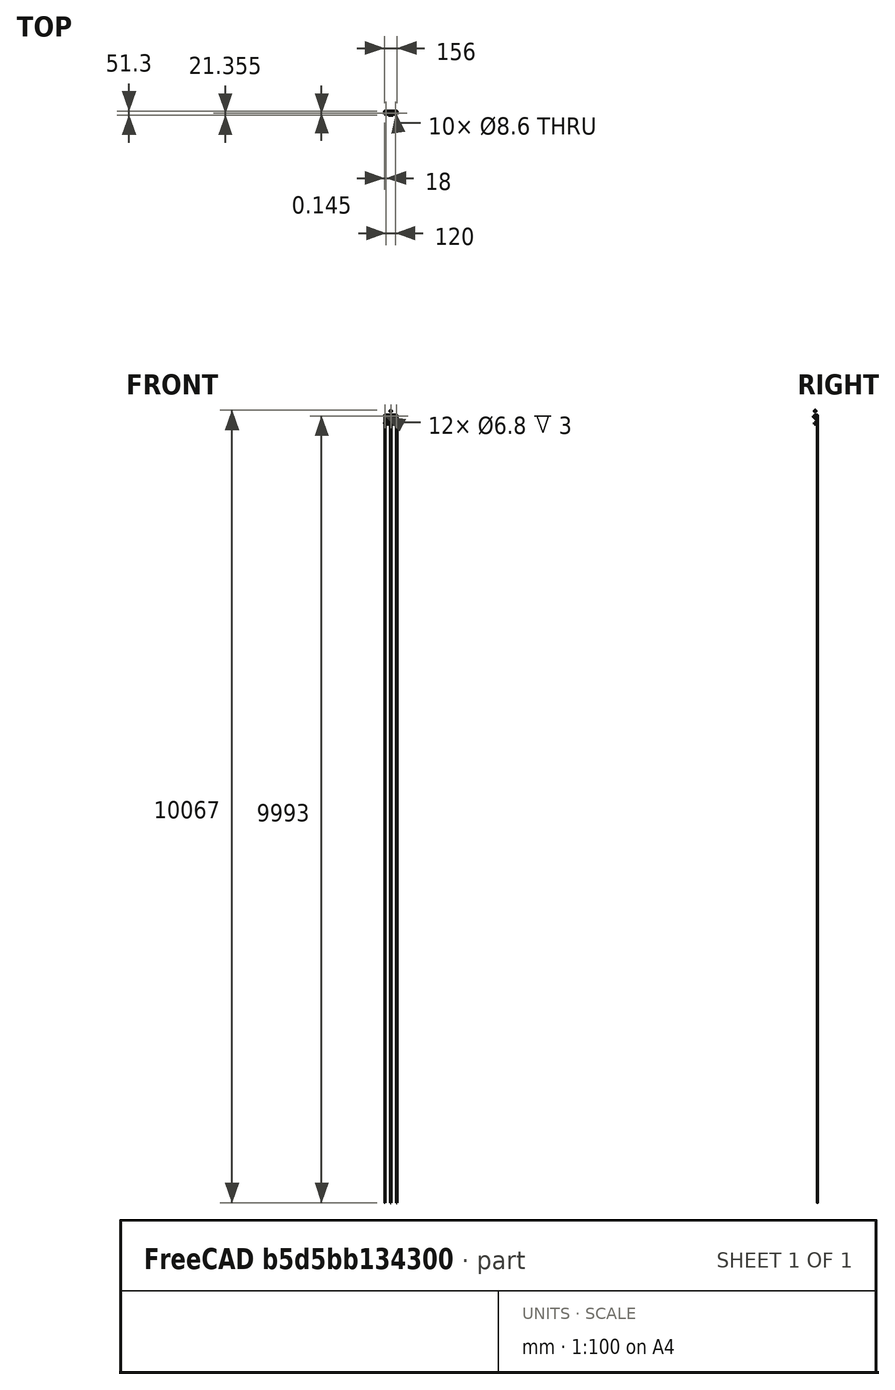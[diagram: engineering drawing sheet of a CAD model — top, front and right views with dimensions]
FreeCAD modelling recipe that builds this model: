
FCSTD DOCUMENT  (FreeCAD 0.15R4671 (Git))
Label: ZRodHolderEnd
License: All rights reserved
LicenseURL: http://en.wikipedia.org/wiki/All_rights_reserved
objects: Sketcher::SketchObject×7, PartDesign::Fillet×6, PartDesign::Pocket×5, Part::Feature×3, PartDesign::Pad×2, PartDesign::Chamfer×1, Mesh::Feature×1
note: 31 computed .brp shape members not serialized (recipe doc carries the construction recipe); baked Part::Feature solids carry a one-line shape summary decoded from their .brp

FEATURE [Part::Feature] Part__Feature  label="TempZMotorEnd"
  shape: bbox 155 x 49.5 x 115 mm, 106 faces (baked)
FEATURE [Part::Feature] _mmBrasNut  label="8mmBrassNut"
  Placement = pos=(0,-28.14,59) rot=(0.707107,0,0.707107;3.14159rad)
  shape: bbox 22 x 22 x 16.42 mm, 29 faces (baked)
FEATURE [Sketcher::SketchObject] Sketch
  Placement = pos=(0,0,0) rot=(-1,0,0;4.71239rad)
  sketch-geometry (4):
    g0: LineSegment StartX=-78 StartY=7.5 StartZ=0 EndX=78 EndY=7.5 EndZ=0
    g1: LineSegment StartX=78 StartY=7.5 StartZ=0 EndX=78 EndY=-7.5 EndZ=0
    g2: LineSegment StartX=78 StartY=-7.5 StartZ=0 EndX=-78 EndY=-7.5 EndZ=0
    g3: LineSegment StartX=-78 StartY=-7.5 StartZ=0 EndX=-78 EndY=7.5 EndZ=0
  constraints (12):
    c: Coincident(g0,g1)
    c: Coincident(g1,g2)
    c: Coincident(g2,g3)
    c: Coincident(g3,g0)
    c: Horizontal(g0)
    c: Horizontal(g2)
    c: Vertical(g1)
    c: Vertical(g3)
    c: DistanceY(g1,g0) = 15
    c: DistanceY(g-1,g1) = -7.5
    c: DistanceX(g1,g2) = -156
    c: DistanceX(g-1,g2) = -78
FEATURE [PartDesign::Pad] Pad
  Length = 36
  Length2 = 100
  Placement = pos=(0,0,0) rot=(-1,0,0;4.71239rad)
  Sketch = -> Sketch
  Type = 0
FEATURE [Sketcher::SketchObject] Sketch001
  Placement = pos=(0,0,7.5) rot=(0,0,1;3.14159rad)
  Support = -> Pad [Face1]
  sketch-geometry (16):
    g0: LineSegment StartX=-80 StartY=7 StartZ=0 EndX=-68 EndY=7 EndZ=0
    g1: LineSegment StartX=-68 StartY=7 StartZ=0 EndX=-68 EndY=37 EndZ=0
    g2: LineSegment StartX=-68 StartY=37 StartZ=0 EndX=-52 EndY=37 EndZ=0
    g3: LineSegment StartX=-52 StartY=37 StartZ=0 EndX=-52 EndY=28 EndZ=0
    g4: LineSegment StartX=-52 StartY=28 StartZ=0 EndX=-32 EndY=7 EndZ=0
    g5: LineSegment StartX=-32 StartY=7 StartZ=0 EndX=32 EndY=7 EndZ=0
    g6: LineSegment StartX=32 StartY=7 StartZ=0 EndX=52 EndY=28 EndZ=0
    g7: LineSegment StartX=52 StartY=28 StartZ=0 EndX=52 EndY=37 EndZ=0
    g8: LineSegment StartX=52 StartY=37 StartZ=0 EndX=68 EndY=37 EndZ=0
    g9: LineSegment StartX=68 StartY=37 StartZ=0 EndX=68 EndY=7 EndZ=0
    g10: LineSegment StartX=68 StartY=7 StartZ=0 EndX=80 EndY=7 EndZ=0
    g11: LineSegment StartX=80 StartY=7 StartZ=0 EndX=80 EndY=53.5948 EndZ=0
    g12: LineSegment StartX=80 StartY=53.5948 StartZ=0 EndX=-80 EndY=53.5948 EndZ=0
    g13: LineSegment StartX=-80 StartY=53.5948 StartZ=0 EndX=-80 EndY=7 EndZ=0
    g14: Circle CenterX=-60 CenterY=28 CenterZ=0 NormalX=0 NormalY=0 NormalZ=1 Radius=4.3
    g15: Circle CenterX=60 CenterY=28 CenterZ=0 NormalX=0 NormalY=0 NormalZ=1 Radius=4.3
  constraints (27):
    c: Coincident(g0,g1)
    c: Coincident(g1,g2)
    c: Coincident(g2,g3)
    c: Coincident(g3,g4)
    c: Coincident(g4,g5)
    c: Coincident(g5,g6)
    c: Coincident(g6,g7)
    c: Coincident(g7,g8)
    c: Coincident(g8,g9)
    c: Coincident(g9,g10)
    c: Coincident(g10,g11)
    c: Coincident(g11,g12)
    c: Coincident(g12,g13)
    c: Coincident(g13,g0)
    c: Horizontal(g12)
    c: Vertical(g11)
    c: Vertical(g13)
    c: Vertical(g9)
    c: Vertical(g7)
    c: Vertical(g3)
    c: Vertical(g1)
    c: Horizontal(g2)
    c: Horizontal(g8)
    c: Horizontal(g10)
    c: Horizontal(g0)
    c: Radius(g15) = 4.3
    c: Equal(g15,g14)
FEATURE [PartDesign::Pocket] Pocket
  Length = 5
  Placement = pos=(0,0,0) rot=(-1,0,0;4.71239rad)
  Sketch = -> Sketch001
  Type = 1
FEATURE [PartDesign::Chamfer] Chamfer
  Base = -> Pocket [Edge24,Edge27,Edge36,Edge39]
  Placement = pos=(0,0,0) rot=(-1,0,0;4.71239rad)
  Size = 4
FEATURE [PartDesign::Fillet] Fillet
  Base = -> Chamfer [Edge21,Edge24,Edge28,Edge33,Edge52,Edge54,Edge51,Edge46]
  Placement = pos=(0,0,0) rot=(-1,0,0;4.71239rad)
  Radius = 2
FEATURE [PartDesign::Fillet] Fillet001
  Base = -> Fillet [Edge72,Edge68,Edge64,Edge60,Edge30,Edge51]
  Placement = pos=(0,0,0) rot=(-1,0,0;4.71239rad)
  Radius = 2
FEATURE [Sketcher::SketchObject] Sketch002
  Placement = pos=(0,-7,0) rot=(1,0,0;1.5708rad)
  Support = -> Fillet001 [Face26]
  sketch-geometry (3):
    g0: Circle CenterX=0 CenterY=0 CenterZ=0 NormalX=0 NormalY=0 NormalZ=1 Radius=1.8
    g1: Circle CenterX=74 CenterY=0 CenterZ=0 NormalX=0 NormalY=0 NormalZ=1 Radius=1.8
    g2: Circle CenterX=-74 CenterY=0 CenterZ=0 NormalX=0 NormalY=0 NormalZ=1 Radius=1.8
  constraints (3):
    c: Radius(g2) = 1.8
    c: Equal(g2,g0)
    c: Equal(g2,g1)
FEATURE [PartDesign::Pocket] Pocket001
  Length = 5
  Placement = pos=(0,0,0) rot=(-1,0,0;4.71239rad)
  Sketch = -> Sketch002
  Type = 1
FEATURE [Sketcher::SketchObject] Sketch003
  Placement = pos=(0,-7,0) rot=(1,0,0;1.5708rad)
  Support = -> Pocket001 [Face26]
  sketch-geometry (3):
    g0: Circle CenterX=0 CenterY=0 CenterZ=0 NormalX=0 NormalY=0 NormalZ=1 Radius=3.4
    g1: Circle CenterX=74 CenterY=0 CenterZ=0 NormalX=0 NormalY=0 NormalZ=1 Radius=3.4
    g2: Circle CenterX=-74 CenterY=0 CenterZ=0 NormalX=0 NormalY=0 NormalZ=1 Radius=3.4
  constraints (3):
    c: Radius(g2) = 3.4
    c: Equal(g2,g0)
    c: Equal(g2,g1)
FEATURE [PartDesign::Pocket] Pocket002
  Length = 3
  Placement = pos=(0,0,0) rot=(-1,0,0;4.71239rad)
  Sketch = -> Sketch003
  Type = 0
FEATURE [PartDesign::Fillet] Fillet002
  Base = -> Pocket002 [Edge59,Edge10,Edge48,Edge6]
  Placement = pos=(0,0,0) rot=(-1,0,0;4.71239rad)
  Radius = 4
FEATURE [Mesh::Feature] MicroSwitch
  Placement = pos=(68.3,-20,3) rot=(0.57735,0.57735,0.57735;2.0944rad)
FEATURE [Sketcher::SketchObject] Sketch004
  Placement = pos=(68,0,0) rot=(0.707107,0,0.707107;3.14159rad)
  Support = -> Fillet002 [Face6]
  sketch-geometry (2):
    g0: Circle CenterX=0.25 CenterY=24.5 CenterZ=0 NormalX=0 NormalY=0 NormalZ=1 Radius=1
    g1: Circle CenterX=0.25 CenterY=15 CenterZ=0 NormalX=0 NormalY=0 NormalZ=1 Radius=1
  constraints (2):
    c: Radius(g1) = 1
    c: Equal(g1,g0)
FEATURE [PartDesign::Pocket] Pocket003  label="ZRodHolderMiddle_1"
  Length = 4
  Placement = pos=(0,0,0) rot=(-1,0,0;4.71239rad)
  Sketch = -> Sketch004
  Type = 0
FEATURE [PartDesign::Fillet] Fillet003
  Base = -> Pocket003 [Edge26]
  Placement = pos=(0,0,0) rot=(-1,0,0;4.71239rad)
  Radius = 1
FEATURE [Part::Feature] Fillet004  label="ZRodHolderMiddle_2"
  shape: bbox 156.7 x 36 x 15.66 mm, 122 faces (baked)
FEATURE [Sketcher::SketchObject] Sketch005
  Placement = pos=(0,0,7.5) rot=(0,0,1;0rad)
  Support = -> Fillet004 [Face1]
  sketch-geometry (8):
    g0: LineSegment StartX=65 StartY=-6 StartZ=0 EndX=36 EndY=-6 EndZ=0
    g1: LineSegment StartX=36 StartY=-6 StartZ=0 EndX=51 EndY=-21 EndZ=0
    g2: LineSegment StartX=51 StartY=-21 StartZ=0 EndX=65 EndY=-21 EndZ=0
    g3: LineSegment StartX=65 StartY=-21 StartZ=0 EndX=65 EndY=-6 EndZ=0
    g4: LineSegment StartX=-37 StartY=-7 StartZ=0 EndX=-65 EndY=-7 EndZ=0
    g5: LineSegment StartX=-65 StartY=-7 StartZ=0 EndX=-65 EndY=-21 EndZ=0
    g6: LineSegment StartX=-65 StartY=-21 StartZ=0 EndX=-51 EndY=-21 EndZ=0
    g7: LineSegment StartX=-51 StartY=-21 StartZ=0 EndX=-37 EndY=-7 EndZ=0
  constraints (8):
    c: Coincident(g0,g1)
    c: Coincident(g1,g2)
    c: Coincident(g2,g3)
    c: Coincident(g3,g0)
    c: Coincident(g4,g5)
    c: Coincident(g5,g6)
    c: Coincident(g6,g7)
    c: Coincident(g7,g4)
FEATURE [PartDesign::Pocket] Pocket004
  Length = 12
  Sketch = -> Sketch005
  Type = 0
FEATURE [PartDesign::Fillet] Fillet005
  Base = -> Pocket004 [Edge128,Edge134,Edge132,Edge130,Edge118,Edge120,Edge122,Edge124]
  Radius = 2
FEATURE [PartDesign::Fillet] Fillet006  label="ZRodHolderMiddle"
  Base = -> Fillet005 [Edge6,Edge45]
  Radius = 1
FEATURE [Sketcher::SketchObject] Sketch006
  Placement = pos=(0,0,-7.5) rot=(1,0,0;3.14159rad)
  Support = -> Fillet006 [Face66]
  sketch-geometry (2):
    g0: Circle CenterX=-60 CenterY=28 CenterZ=0 NormalX=0 NormalY=0 NormalZ=1 Radius=6
    g1: Circle CenterX=60 CenterY=28 CenterZ=0 NormalX=0 NormalY=0 NormalZ=1 Radius=6
FEATURE [PartDesign::Pad] Pad001  label="ZRodHolderEnd"
  Length = 5
  Length2 = 100
  Reversed = true
  Sketch = -> Sketch006
  Type = 0
